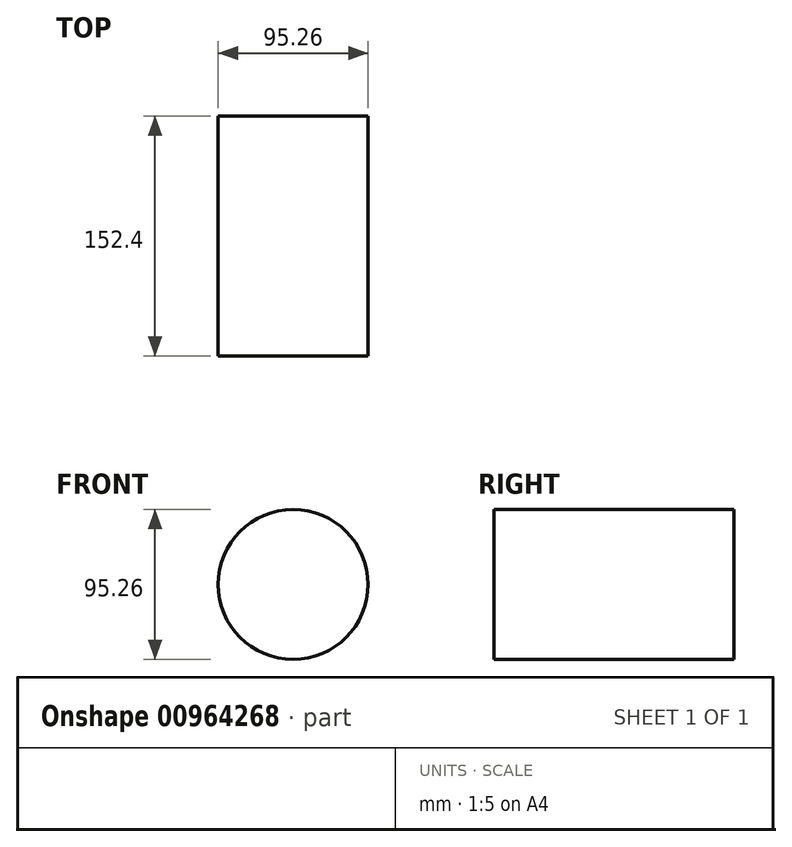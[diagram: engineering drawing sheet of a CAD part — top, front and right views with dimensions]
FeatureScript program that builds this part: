
annotation { "Feature Type Name" : "Feature", "Feature Type Description" : "" }
export const myFeature = defineFeature(function(context is Context, id is Id, definition is map)
    precondition{}
    {
        {
            var Q0;
            Q0=qCreatedBy(makeId("Front.planeOp"),FACE);
            var sketch = newSketch(context, id + "F0", { "sketchPlane" : qUnion([Q0])});
            skCircle(sketch, "E0", {"center": v(0, 0) * mm, "radius": 47.63 * mm});
            skSolve(sketch);
        }
        {
            var Q0;
            Q0=makeQuery(id+"F0.imprint","IMPRINT",FACE,{"disambiguationData":[TD([[makeQuery(id+"F0.imprint","IMPRINT",EDGE,{"derivedFrom":sQuery(id+"F0.wireOp",EDGE,"E0")}),1.0]])]});
            extrude(context, id + "F1", {"entities" : qUnion([Q0]), "depth" : 152.4 * mm, "offsetDistance" : 25.4 * mm});
        }
    });
